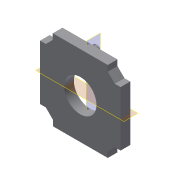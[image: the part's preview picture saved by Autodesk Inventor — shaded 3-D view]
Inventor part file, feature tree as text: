
AUTODESK INVENTOR PART (.ipt)
format: ipt  version: 2022 (Build 260153000, 153)  size: 246,784 bytes
history: native  units: mm
features: reference x10, other x8, extrude x5, sketch x5, plane x3, projected_geometry x3
ambient origin geometry x8: Origin, YZ Plane, XZ Plane, XY Plane, X Axis, Y Axis, Z Axis, Center Point
bodies: Solid1 (feature_tree)
feature tree (34):
  plane  "Work Plane1"
  extrude  "Extrusion1"  Depth=6.0mm
  extrude  "IM_offset"  Depth=53.8mm
  plane  "Arbeitsebene5"
  plane  "Arbeitsebene6"
  extrude  "Extrusion26"  Depth=45.0mm
  extrude  "Extrusion27"  Depth=20.0mm
  extrude  "Extrusion28"  Depth=1.0mm
  sketch  "Sketch1"  dims[d10=6.0mm d11=0.0mm d18=53.8mm]
  reference  "Reference1"
  reference  "Reference2"
  reference  "Reference3"
  reference  "Reference4"
  reference  "Reference9"
  reference  "Reference20"
  reference  "Reference21"
  reference  "Reference22"
  reference  "Reference23"
  reference  "Reference24"
  sketch  "Skizze4"  dims[d19=45.0deg d20=53.8mm]
  projected_geometry  "Projizierte Kontur1"
  sketch  "Skizze31"  dims[d21=45.0mm d22=45.0mm]
  projected_geometry  "Projizierte Kontur17"
  sketch  "Skizze32"  dims[d30=20.0mm d31=20.0mm]
  sketch  "Skizze33"  dims[d32=2.8mm d33=2.8mm d34=2.8mm d35=3.0mm d36=0.1mm d37=0.1mm d38=0.1mm d39=0.1mm d40=0.2mm d41=10.0mm d42=0.0mm d181=20.0mm d182=10.0mm d183=0.0mm d184=30.0mm d185=10.0mm d186=5.0mm d187=5.0mm d188=5.0mm d189=8.0mm d190=8.0mm d191=8.0mm d192=4.0mm d193=0.0mm d194=0.5mm d195=0.5mm d196=0.5mm d197=1.0mm d198=0.0mm d160=0.5mm d161=0.872665mm d162=0.5mm d163=0.872665mm]
  projected_geometry  "Projizierte Kontur18"
  other  "Assembly_Cube_v2_Thorlabs.iam"
  other  "10_Cube_Base:1"
  other  "00_Base_v0:1"
  other  "Assembly_Cube_Kinematic_Mirrormount_v2.iam"
  other  "Assembly_Cube_empty_1x1_v2:1"
  other  "10_Cube_1x1_v2:1"
  other  "10_Lid_1x1_v2:1"
  other  "10_Cube_Lid:1"
